# Revit family: Water_Heaters_HAJDU_HAJDU-PT-HC_
name_source: partatom
category: Mechanical Equipment
units: mm (PartAtom-declared; Revit-internal decimal feet)

## family parameters
Always vertical = Yes
Classification = None
Cut with Voids When Loaded = No
Maintain Annotation Orientation = No
OmniClass Number = 23.31.29.13
OmniClass Title = Hot Water Tank Heaters
Part Type = Normal
Room Calculation Point = No
Round Connector Dimension = Use Diameter
Shared = No
Work Plane-Based = Yes

## types (2) — shared parameters
Case Material = Hajdu - Felület - Fehér
Csatlakozó magassága "C" = 247 mm
Default Elevation = 1219.2 mm  [stored 4 ft]
Description = A PT HC típusok a fűtési-hűtési rendszerek energiatárolói. Elsősorban hőszivattyús rendszerekhez ajánljuk. A puffertárolót acéltartály, poliuretán hab szigetelés, műanyagköpeny és - fedél alkotja. 100 és 200 literes, üres kivitelben készülnek.
Felso csonk = 38.1 mm  [stored 0.125 ft]
Hoérzékelo csonk = 12.7 mm  [stored 0.0416667 ft]
Manufacturer = HAJDU
Product Page URL = https://hajdurt.hu
Rádiusz = 273 mm  [stored 0.895669 ft]
URL = https://hajdurt.hu
Vízcsatlakozás = 38.1 mm  [stored 0.125 ft]
Átméro = 546 mm  [stored 1.79134 ft]
Üzemi nyomás tartály = 0.3 MPa

## per-type parameters (varying)
| type | Csatlakozó magassága "A" | Csatlakozó magassága "B" | Csatlakozó magassága "D" | Energiahatékonysági osztály | Magasság | Névleges urtartalom | Tárolási veszteség | Tömeg |
| PT HC 100 | 628 mm  [stored 2.06037 ft] | 433 mm | 614 mm  [stored 2.01444 ft] | B | 874 mm  [stored 2.86745 ft] | 100 l | 39 W | 28.00 kg |
| PT HC 200 | 1228 mm  [stored 4.02887 ft] | 913 mm | 1214 mm  [stored 3.98294 ft] | C | 1474 mm  [stored 4.83596 ft] | 200 l | 65 W | 40.00 kg |

note: column(s) folded — value = type name in every type: Model

note: [stored X ft] marks values corroborated as IEEE doubles in the binary element streams (Revit-internal decimal feet)

## geometry (parser evidence)
native form markers: Sweep x4
no freeform markers — native parametric forms only
